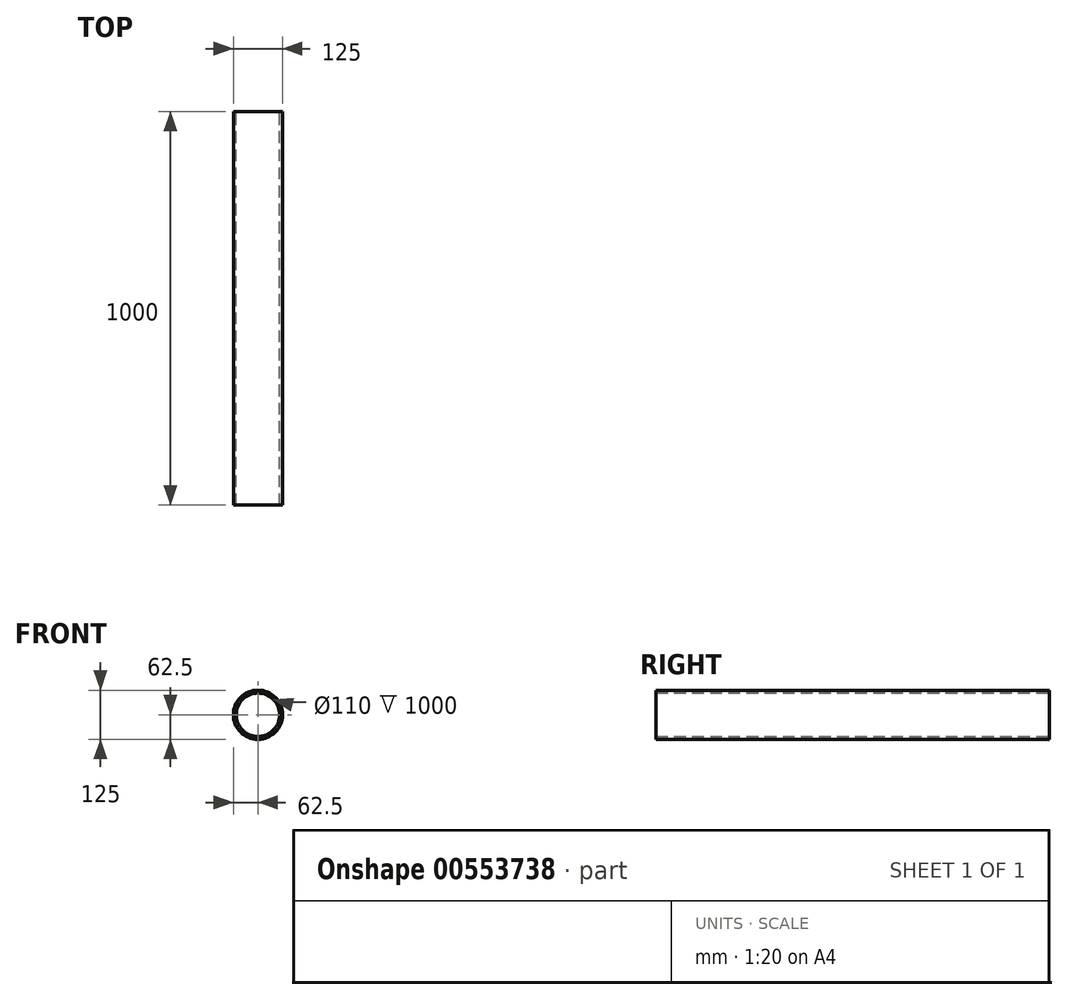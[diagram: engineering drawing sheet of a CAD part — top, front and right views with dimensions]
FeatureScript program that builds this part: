
annotation { "Feature Type Name" : "Feature", "Feature Type Description" : "" }
export const myFeature = defineFeature(function(context is Context, id is Id, definition is map)
    precondition{}
    {
        {
            var Q0;
            Q0=qCreatedBy(makeId("Front.planeOp"),FACE);
            var sketch = newSketch(context, id + "F0", { "sketchPlane" : qUnion([Q0])});
            skCircle(sketch, "E0", {"center": v(0, 0) * mm, "radius": 62.5 * mm});
            skCircle(sketch, "E1", {"center": v(0, 0) * mm, "radius": 55 * mm});
            skSolve(sketch);
        }
        {
            var Q0;
            Q0=makeQuery(id+"F0.imprint","IMPRINT",FACE,{"disambiguationData":[TD([[makeQuery(id+"F0.imprint","IMPRINT",EDGE,{"derivedFrom":sQuery(id+"F0.wireOp",EDGE,"E0")}),1.0]])]});
            extrude(context, id + "F1", {"entities" : qUnion([Q0]), "endBound" : BoundingType.SYMMETRIC, "depth" : 1000 * mm, "offsetDistance" : 25 * mm});
        }
    });
